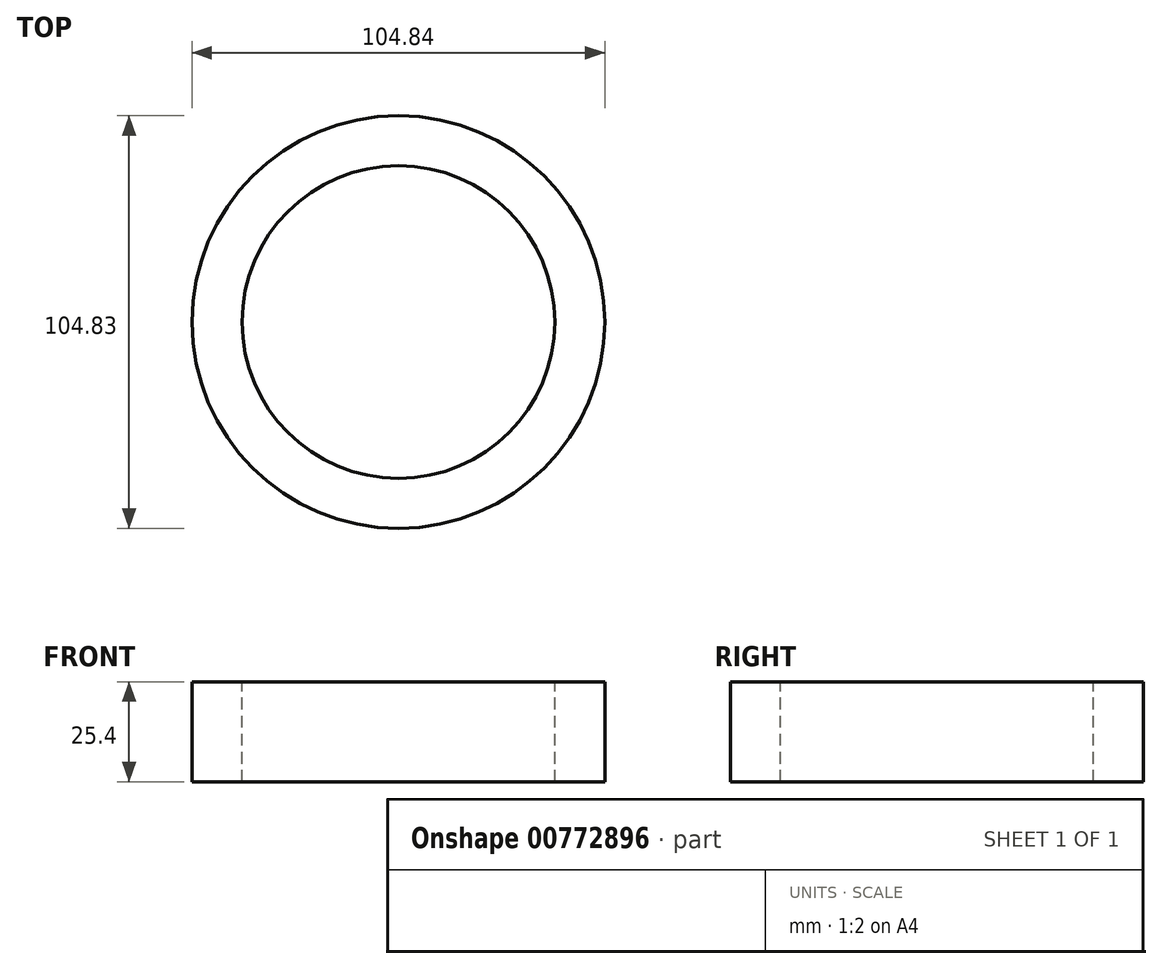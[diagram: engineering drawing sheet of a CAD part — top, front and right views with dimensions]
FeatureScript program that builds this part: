
annotation { "Feature Type Name" : "Feature", "Feature Type Description" : "" }
export const myFeature = defineFeature(function(context is Context, id is Id, definition is map)
    precondition{}
    {
        {
            var Q0;
            Q0=qCreatedBy(makeId("Top.planeOp"),FACE);
            var sketch = newSketch(context, id + "F0", { "sketchPlane" : qUnion([Q0])});
            skCircle(sketch, "E0", {"center": v(0, 2.94) * mm, "radius": 39.72 * mm});
            skCircle(sketch, "E1.0", {"center": v(0, 2.94) * mm, "radius": 52.42 * mm});
            skSolve(sketch);
        }
        {
            var Q0;
            Q0 = qConstructionFilter(qBodyType(qCreatedBy(id + "F0" ,EDGE), BodyType.WIRE), ConstructionObject.NO);
            extrude(context, id + "F1", {"bodyType" : ToolBodyType.SURFACE, "surfaceEntities" : qUnion([Q0]), "depth" : 25.4 * mm, "offsetDistance" : 25.4 * mm});
        }
    });
